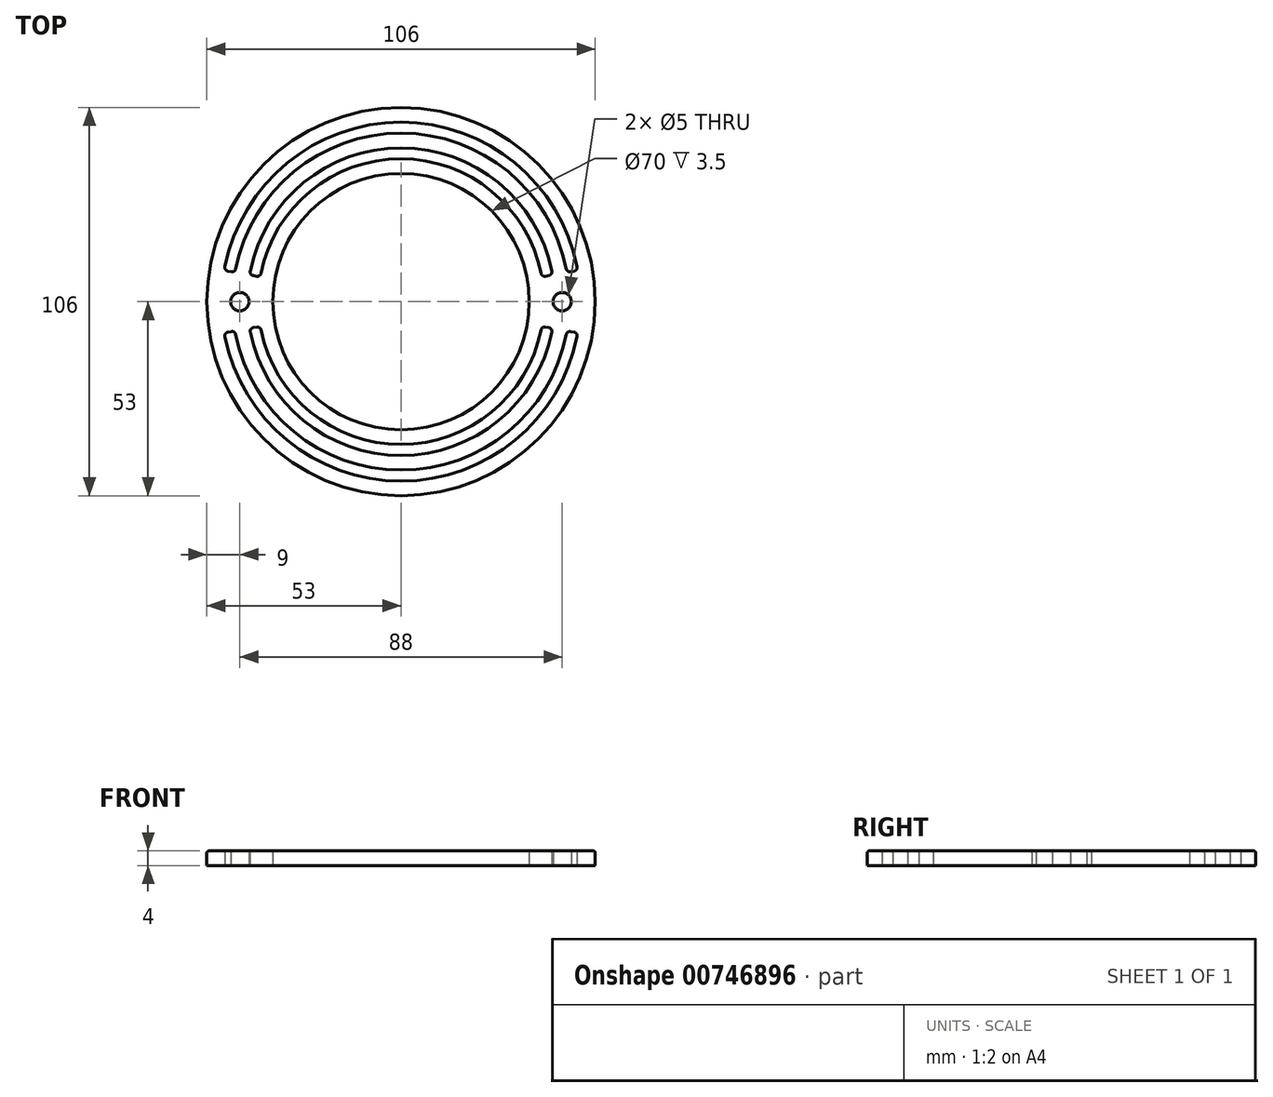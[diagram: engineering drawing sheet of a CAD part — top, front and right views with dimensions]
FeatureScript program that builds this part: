
annotation { "Feature Type Name" : "Feature", "Feature Type Description" : "" }
export const myFeature = defineFeature(function(context is Context, id is Id, definition is map)
    precondition{}
    {
        {
            var Q0;
            Q0=qCreatedBy(makeId("Top.planeOp"),FACE);
            var sketch = newSketch(context, id + "F0", { "sketchPlane" : qUnion([Q0])});
            skCircle(sketch, "E0", {"center": v(0, 0) * mm, "radius": 35 * mm});
            skCircle(sketch, "E1", {"center": v(0, 0) * mm, "radius": 53 * mm});
            skLineSegment(sketch, "E2", {"start": v(75.1, 0) * mm, "end": v(-91.1, 0) * mm, "construction": true});
            skCircle(sketch, "E3", {"center": v(0, 0) * mm, "radius": 44 * mm, "construction": true});
            skCircle(sketch, "E4", {"center": v(-44, 0) * mm, "radius": 2.5 * mm});
            skCircle(sketch, "E5", {"center": v(44, 0) * mm, "radius": 2.5 * mm});
            skArc(sketch, "E6", {"start": v(-38.4, -6.77) * mm, "mid": v(0, -39) * mm, "end": v(38.4, -6.77) * mm});
            skArc(sketch, "E7", {"start": v(-41.36, -7.3) * mm, "mid": v(0, -42) * mm, "end": v(41.36, -7.3) * mm});
            skArc(sketch, "E8", {"start": v(-45.3, -7.99) * mm, "mid": v(0, -46) * mm, "end": v(45.3, -7.99) * mm});
            skArc(sketch, "E9", {"start": v(-48.26, -8.5) * mm, "mid": v(0, -49) * mm, "end": v(48.26, -8.5) * mm});
            skLineSegment(sketch, "E10", {"start": v(0, -73.98) * mm, "end": v(0, 75.64) * mm, "construction": true});
            skLineSegment(sketch, "E11.trimOffspring", {"start": v(45.3, -7.99) * mm, "end": v(48.26, -8.5) * mm});
            skLineSegment(sketch, "E12.trimOffspring", {"start": v(38.4, -6.77) * mm, "end": v(41.36, -7.3) * mm});
            skLineSegment(sketch, "E13.trimOffspring", {"start": v(-45.3, -7.99) * mm, "end": v(-48.26, -8.5) * mm});
            skLineSegment(sketch, "E14.trimOffspring", {"start": v(-38.4, -6.77) * mm, "end": v(-41.36, -7.3) * mm});
            skLineSegment(sketch, "E15.MirrorCS", {"start": v(-45.3, 7.99) * mm, "end": v(-48.26, 8.5) * mm});
            skArc(sketch, "E16.MirrorCS", {"start": v(-48.26, 8.5) * mm, "mid": v(0, 49) * mm, "end": v(48.26, 8.5) * mm});
            skArc(sketch, "E17.MirrorCS", {"start": v(-45.3, 7.99) * mm, "mid": v(0, 46) * mm, "end": v(45.3, 7.99) * mm});
            skLineSegment(sketch, "E18.MirrorCS", {"start": v(45.3, 7.99) * mm, "end": v(48.26, 8.5) * mm});
            skArc(sketch, "E19.MirrorCS", {"start": v(-41.36, 7.3) * mm, "mid": v(0, 42) * mm, "end": v(41.36, 7.3) * mm});
            skLineSegment(sketch, "E20.MirrorCS", {"start": v(38.4, 6.77) * mm, "end": v(41.36, 7.3) * mm});
            skArc(sketch, "E21.MirrorCS", {"start": v(-38.4, 6.77) * mm, "mid": v(0, 39) * mm, "end": v(38.4, 6.77) * mm});
            skLineSegment(sketch, "E22.MirrorCS", {"start": v(-38.4, 6.77) * mm, "end": v(-41.36, 7.3) * mm});
            skSolve(sketch);
        }
        {
            var Q0;
            Q0 = qSketchRegion(id + "F0", true);
            extrude(context, id + "F1", {"entities" : qUnion([Q0]), "depth" : 4 * mm, "offsetDistance" : 25 * mm});
        }
        {
            var Q0;
            Q0=makeQuery(id+"F1.opExtrude","SWEPT_EDGE",EDGE,{"disambiguationData":[OSD([sQuery(id+"F0.wireOp",EDGE,"E15.MirrorCS"),sQuery(id+"F0.wireOp",EDGE,"E16.MirrorCS")])]});
            var Q1;
            Q1=makeQuery(id+"F1.opExtrude","SWEPT_EDGE",EDGE,{"disambiguationData":[OSD([sQuery(id+"F0.wireOp",EDGE,"E15.MirrorCS"),sQuery(id+"F0.wireOp",EDGE,"E17.MirrorCS")])]});
            var Q2;
            Q2=makeQuery(id+"F1.opExtrude","SWEPT_EDGE",EDGE,{"disambiguationData":[OSD([sQuery(id+"F0.wireOp",EDGE,"E21.MirrorCS"),sQuery(id+"F0.wireOp",EDGE,"E22.MirrorCS")])]});
            var Q3;
            Q3=makeQuery(id+"F1.opExtrude","SWEPT_EDGE",EDGE,{"disambiguationData":[OSD([sQuery(id+"F0.wireOp",EDGE,"E19.MirrorCS"),sQuery(id+"F0.wireOp",EDGE,"E22.MirrorCS")])]});
            var Q4;
            Q4=makeQuery(id+"F1.opExtrude","SWEPT_EDGE",EDGE,{"disambiguationData":[OSD([sQuery(id+"F0.wireOp",EDGE,"E6"),sQuery(id+"F0.wireOp",EDGE,"E14.trimOffspring")])]});
            var Q5;
            Q5=makeQuery(id+"F1.opExtrude","SWEPT_EDGE",EDGE,{"disambiguationData":[OSD([sQuery(id+"F0.wireOp",EDGE,"E8"),sQuery(id+"F0.wireOp",EDGE,"E13.trimOffspring")])]});
            var Q6;
            Q6=makeQuery(id+"F1.opExtrude","SWEPT_EDGE",EDGE,{"disambiguationData":[OSD([sQuery(id+"F0.wireOp",EDGE,"E7"),sQuery(id+"F0.wireOp",EDGE,"E14.trimOffspring")])]});
            var Q7;
            Q7=makeQuery(id+"F1.opExtrude","SWEPT_EDGE",EDGE,{"disambiguationData":[OSD([sQuery(id+"F0.wireOp",EDGE,"E9"),sQuery(id+"F0.wireOp",EDGE,"E13.trimOffspring")])]});
            var Q8;
            Q8=makeQuery(id+"F1.opExtrude","SWEPT_EDGE",EDGE,{"disambiguationData":[OSD([sQuery(id+"F0.wireOp",EDGE,"E6"),sQuery(id+"F0.wireOp",EDGE,"E12.trimOffspring")])]});
            var Q9;
            Q9=makeQuery(id+"F1.opExtrude","SWEPT_EDGE",EDGE,{"disambiguationData":[OSD([sQuery(id+"F0.wireOp",EDGE,"E8"),sQuery(id+"F0.wireOp",EDGE,"E11.trimOffspring")])]});
            var Q10;
            Q10=makeQuery(id+"F1.opExtrude","SWEPT_EDGE",EDGE,{"disambiguationData":[OSD([sQuery(id+"F0.wireOp",EDGE,"E7"),sQuery(id+"F0.wireOp",EDGE,"E12.trimOffspring")])]});
            var Q11;
            Q11=makeQuery(id+"F1.opExtrude","SWEPT_EDGE",EDGE,{"disambiguationData":[OSD([sQuery(id+"F0.wireOp",EDGE,"E9"),sQuery(id+"F0.wireOp",EDGE,"E11.trimOffspring")])]});
            var Q12;
            Q12=makeQuery(id+"F1.opExtrude","SWEPT_EDGE",EDGE,{"disambiguationData":[OSD([sQuery(id+"F0.wireOp",EDGE,"E19.MirrorCS"),sQuery(id+"F0.wireOp",EDGE,"E20.MirrorCS")])]});
            var Q13;
            Q13=makeQuery(id+"F1.opExtrude","SWEPT_EDGE",EDGE,{"disambiguationData":[OSD([sQuery(id+"F0.wireOp",EDGE,"E16.MirrorCS"),sQuery(id+"F0.wireOp",EDGE,"E18.MirrorCS")])]});
            var Q14;
            Q14=makeQuery(id+"F1.opExtrude","SWEPT_EDGE",EDGE,{"disambiguationData":[OSD([sQuery(id+"F0.wireOp",EDGE,"E20.MirrorCS"),sQuery(id+"F0.wireOp",EDGE,"E21.MirrorCS")])]});
            var Q15;
            Q15=makeQuery(id+"F1.opExtrude","SWEPT_EDGE",EDGE,{"disambiguationData":[OSD([sQuery(id+"F0.wireOp",EDGE,"E17.MirrorCS"),sQuery(id+"F0.wireOp",EDGE,"E18.MirrorCS")])]});
            fillet(context, id + "F2", {"entities" : qUnion([Q0, Q1, Q2, Q3, Q4, Q5, Q6, Q7, Q8, Q9, Q10, Q11, Q12, Q13, Q14, Q15]), "radius" : 1 * mm, "tangentPropagation" : true, "allowEdgeOverflow" : false});
        }
        {
            var Q0;
            Q0=makeQuery(id+"F1.opExtrude","CAP_EDGE",EDGE,{"disambiguationData":[OSD([sQuery(id+"F0.wireOp",EDGE,"E1")])],"isStart":false});
            var Q1;
            Q1=makeQuery(id+"F1.opExtrude","CAP_EDGE",EDGE,{"disambiguationData":[OSD([sQuery(id+"F0.wireOp",EDGE,"E16.MirrorCS")])],"isStart":false});
            var Q2;
            Q2=makeQuery(id+"F1.opExtrude","CAP_EDGE",EDGE,{"disambiguationData":[OSD([sQuery(id+"F0.wireOp",EDGE,"E19.MirrorCS")])],"isStart":false});
            var Q3;
            Q3=makeQuery(id+"F1.opExtrude","CAP_EDGE",EDGE,{"disambiguationData":[OSD([sQuery(id+"F0.wireOp",EDGE,"E5")])],"isStart":false});
            var Q4;
            Q4=makeQuery(id+"F1.opExtrude","CAP_EDGE",EDGE,{"disambiguationData":[OSD([sQuery(id+"F0.wireOp",EDGE,"E9")])],"isStart":false});
            var Q5;
            Q5=makeQuery(id+"F1.opExtrude","CAP_EDGE",EDGE,{"disambiguationData":[OSD([sQuery(id+"F0.wireOp",EDGE,"E7")])],"isStart":false});
            var Q6;
            Q6=makeQuery(id+"F1.opExtrude","CAP_EDGE",EDGE,{"disambiguationData":[OSD([sQuery(id+"F0.wireOp",EDGE,"E4")])],"isStart":false});
            var Q7;
            Q7=makeQuery(id+"F1.opExtrude","CAP_EDGE",EDGE,{"disambiguationData":[OSD([sQuery(id+"F0.wireOp",EDGE,"E0")])],"isStart":false});
            fillet(context, id + "F3", {"entities" : qUnion([Q0, Q1, Q2, Q3, Q4, Q5, Q6, Q7]), "radius" : .5 * mm, "tangentPropagation" : true, "allowEdgeOverflow" : false});
        }
    });
